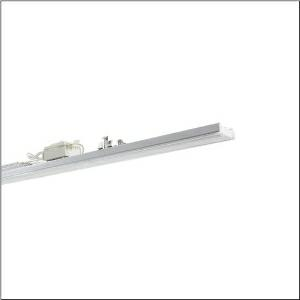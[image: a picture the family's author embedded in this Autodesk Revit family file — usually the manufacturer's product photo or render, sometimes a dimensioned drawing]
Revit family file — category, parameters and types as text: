
# Revit family: licross_11_recessed_ho_51te18dv4m5m
name_source: partatom
category: Lighting Fixtures
units: mm (PartAtom-declared; Revit-internal decimal feet)

## family parameters
Cut with Voids When Loaded = No
Host = Face
Light Source = No
Part Type = Normal
Room Calculation Point = No
Round Connector Dimension = Use Diameter
Shared = No

## types (1)
- --- (1 x LED, 25960 lm, 144.7 W, 4000K)
    Apparent Load = 145 VA
    CIE Flux Codes = 78 94 99 100 100
    Color Rendering = 80
    Color Temperature = 4000K
    Default Elevation = 1800 mm
    Description = Licross 11 Recessed HO, luminaire insert, of sheet steel, galvanised, coil coated, white, length: 2.250mm, width: 66mm, height: 67mm, LED rated luminous flux: 25.960lm, light colour: 840, SDCM (Standard Deviation of Colour Matching)MacAdam ≤ 2 SDCM (initial), control gear: DALI 2, with plug, 5-pole, with phase selection, mains connection: 220..240V, AC, 50/60Hz, rated input power: 145W, internal wiring halogen-free, primary light control with lens, of plastic, primary optical cover: cover, of PMMA, light emission: direct distribution, primary light characteristic: symmetric, protection rating (complete): IP54, insulation class (complete): insulation class I (protective earthing), certification: CE, ENEC, VDE, UKCA, protection symbol: D if used in an environment with non-conductive dust loads with corresponding accessories, impact resistance: IK06, permissible ambient temperature for indoor applications: -40..+35°C, corresponds to IFS (International Featured Standards) requirements for safety and quality in the food industry, reducing of maximum allowable ambient temperature of 5°C with ceiling mounting, LABS conformity tested according to VDMA 24364:2018-05, The light source and the operating device comply with the requirements of the Ecodesign Regulation (EU) 2019/2020 and are replaceable in accordance with this regulation, packaging unit: 1 piece
    Height = 58 mm
    Lamp = 1 x LED
    Lamp Light Flux = 25960 lm
    Lamp Power = 144.7 W
    Lamp count = 1
    Length = 2250 mm
    Luminous efficacy = 179 lm/W
    Manufacturer = Siteco
    ModVariant = No
    Model = 51TE18DV4M5M
    Mounting Place = Ceiling
    Mounting Type = Pendant
    Number of Poles = 1
    OnlyDefault = Yes
    Power Factor = 1
    Product Name = Licross 11 Recessed HO
    Product group = luminaire insert | ceiling pendant
    ProductGroupID = 901
    Protection Class = Protection class I
    Protection Degree = IP 54
    RLX_Detail_Level = 1
    RLX_Emergency_Light_Flux = 0 lm
    RLX_Emergency_Type = 0
    RLX_Emergency_Type_DB = No
    RlxData = <blob elided: 29821 chars, md5=2065c22a>
    Socket = socket
    Standby Power = 0 W
    System Light Flux = 25961 lm
    System Power = 145 W
    Type Comments = factory setting: luminous flux: 100 % | dim-lin: 254 | 665 mA
    Type Image = l_1296930.jpg
    URL = http://relux.com
    VarID = @adj_100901
    Voltage = 0 V
    Weight = 0.00 kg
    Width = 66 mm

## geometry (parser evidence)
native form markers: Blend x4, Sweep x9
no freeform markers — native parametric forms only
